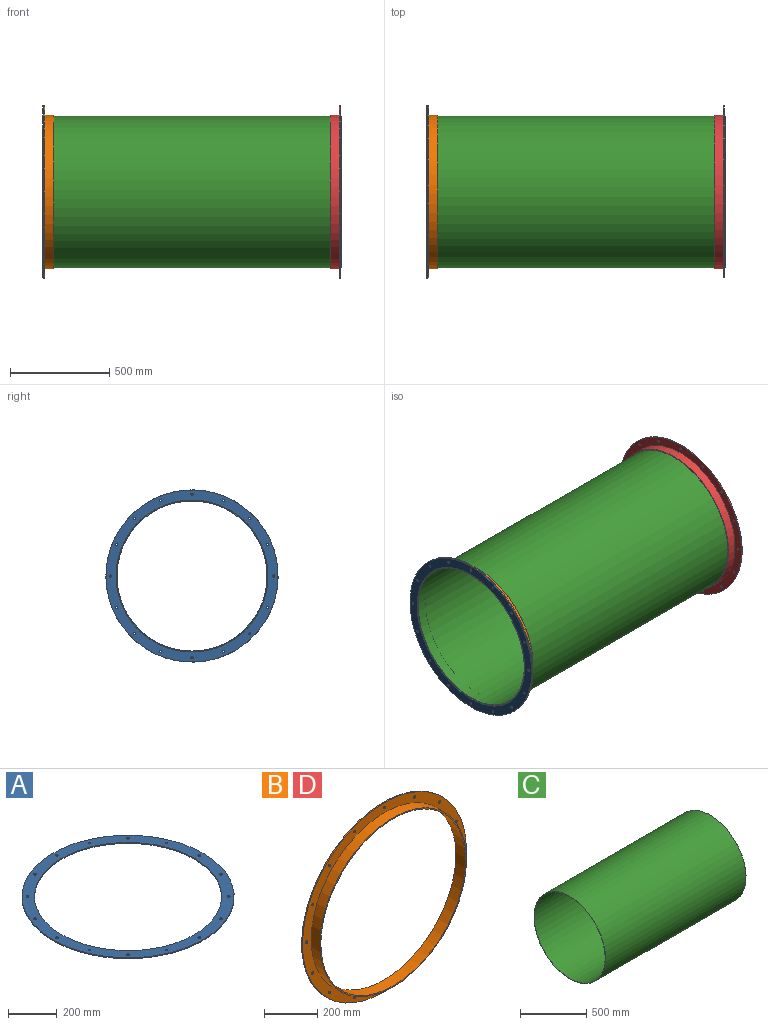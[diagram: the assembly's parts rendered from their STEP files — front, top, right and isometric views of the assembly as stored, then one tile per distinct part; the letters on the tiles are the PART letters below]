
ASSEMBLY  parts=4 mates=3
PART A: 20 faces, bbox 866.9x866.9x4.8 mm
  f0: cylinder r=5.56mm len=11.11mm, axis (0,0,-1), area 166.3mm2, adj f18,f19
  f1: cylinder r=5.56mm len=11.11mm, axis (0,0,-1), area 166.3mm2, adj f18,f19
  f2: cylinder r=5.56mm len=11.11mm, axis (0,0,-1), area 166.3mm2, adj f18,f19
  f3: cylinder r=5.56mm len=11.11mm, axis (0,0,-1), area 166.3mm2, adj f18,f19
  f4: cylinder r=5.56mm len=11.11mm, axis (0,0,-1), area 166.3mm2, adj f18,f19
  f5: cylinder r=5.56mm len=11.11mm, axis (0,0,-1), area 166.3mm2, adj f18,f19
  f6: cylinder r=5.56mm len=11.11mm, axis (0,0,-1), area 166.3mm2, adj f18,f19
  f7: cylinder r=5.56mm len=11.11mm, axis (0,0,-1), area 166.3mm2, adj f18,f19
  f8: cylinder r=5.56mm len=11.11mm, axis (0,0,-1), area 166.3mm2, adj f18,f19
  f9: cylinder r=5.56mm len=11.11mm, axis (0,0,-1), area 166.3mm2, adj f18,f19
  f10: cylinder r=5.56mm len=11.11mm, axis (0,0,-1), area 166.3mm2, adj f18,f19
  f11: cylinder r=5.56mm len=11.11mm, axis (0,0,-1), area 166.3mm2, adj f18,f19
  f12: cylinder r=5.56mm len=11.11mm, axis (0,0,-1), area 166.3mm2, adj f18,f19
  f13: cylinder r=5.56mm len=11.11mm, axis (0,0,-1), area 166.3mm2, adj f18,f19
  f14: cylinder r=5.56mm len=11.11mm, axis (0,0,-1), area 166.3mm2, adj f18,f19
  f15: cylinder r=382.65mm len=765.3mm, axis (0,0,-1), area 11450.3mm2, adj f18,f19
  f16: cylinder r=5.56mm len=11.11mm, axis (0,0,-1), area 166.3mm2, adj f18,f19
  f17: cylinder r=433.45mm len=866.9mm, axis (0,0,-1), area 12970.4mm2, adj f18,f19
  f18: plane 866.9x866.9mm, normal (0,0,1), area 128692.3mm2, adj f0,f1,f2,f3,f4,f5,f6,f7
  f19: plane 866.9x866.9mm, normal (0,0,-1), area 128692.3mm2, adj f0,f1,f2,f3,f4,f5,f6,f7
PART B: 22 faces, bbox 866.9x50.8x866.9 mm
  f0: cylinder r=5.56mm len=11.11mm, axis (0,1,0), area 166.3mm2, adj f17,f18
  f1: cylinder r=5.56mm len=11.11mm, axis (0,1,0), area 166.3mm2, adj f17,f18
  f2: cylinder r=5.56mm len=11.11mm, axis (0,1,0), area 166.3mm2, adj f17,f18
  f3: cylinder r=5.56mm len=11.11mm, axis (0,1,0), area 166.3mm2, adj f17,f18
  f4: cylinder r=5.56mm len=11.11mm, axis (0,1,0), area 166.3mm2, adj f17,f18
  f5: cylinder r=5.56mm len=11.11mm, axis (0,1,0), area 166.3mm2, adj f17,f18
  f6: cylinder r=5.56mm len=11.11mm, axis (0,1,0), area 166.3mm2, adj f17,f18
  f7: cylinder r=5.56mm len=11.11mm, axis (0,1,0), area 166.3mm2, adj f17,f18
  f8: cylinder r=5.56mm len=11.11mm, axis (0,1,0), area 166.3mm2, adj f17,f18
  f9: cylinder r=5.56mm len=11.11mm, axis (0,1,0), area 166.3mm2, adj f17,f18
  f10: cylinder r=5.56mm len=11.11mm, axis (0,1,0), area 166.3mm2, adj f17,f18
  f11: cylinder r=5.56mm len=11.11mm, axis (0,1,0), area 166.3mm2, adj f17,f18
  f12: cylinder r=5.56mm len=11.11mm, axis (0,1,0), area 166.3mm2, adj f17,f18
  f13: cylinder r=5.56mm len=11.11mm, axis (0,1,0), area 166.3mm2, adj f17,f18
  f14: cylinder r=5.56mm len=11.11mm, axis (0,1,0), area 166.3mm2, adj f17,f18
  f15: cylinder r=5.56mm len=11.11mm, axis (0,1,0), area 166.3mm2, adj f17,f18
  f16: cylinder r=433.45mm len=866.9mm, axis (0,1,0), area 12970.4mm2, adj f17,f18
  f17: plane 866.9x866.9mm, normal (0,-1,0), area 117170.7mm2, adj f0,f1,f2,f3,f4,f5,f6,f7
  f18: plane 866.9x866.9mm, normal (0,1,0), area 128692.3mm2, adj f0,f1,f2,f3,f4,f5,f6,f7
  f19: cylinder r=382.65mm len=765.3mm, axis (0,1,0), area 122136.8mm2, adj f18,f21
  f20: cylinder r=387.41mm len=774.83mm, axis (0,1,0), area 112064.1mm2, adj f17,f21
  f21: plane 774.83x774.83mm, normal (0,-1,0), area 11521.6mm2, adj f19,f20
PART C: 4 faces, bbox 1498.6x762x762 mm
  f0: plane 762x762mm, normal (1,0,0), area 8141.6mm2, adj f1,f2
  f1: cylinder r=377.58mm len=1498.6mm, axis (-1,0,0), area 3555321.1mm2, adj f0,f3
  f2: cylinder r=381mm len=1498.6mm, axis (-1,0,0), area 3587489mm2, adj f0,f3
  f3: plane 762x762mm, normal (-1,0,0), area 8141.6mm2, adj f1,f2
PART D: same geometry as B
PLACE A rot(axis=(0.71,0,0.71),180deg) t=(-383.98,196.63,-23.49)mm
PLACE B rot(axis=(0.58,-0.58,0.58),120deg) t=(-379.22,196.63,-23.49)mm
PLACE C t=(-381.6,196.63,-23.49)mm
PLACE D rot(axis=(0.58,0.58,-0.58),120deg) t=(1113.83,196.63,-23.49)mm
MATE fastened D.f19 <-> C.f2  axis (1,0,0) through (1113.83,196.63,-23.49)mm
MATE fastened A.f15 <-> B.f19  axis (1,0,0) through (-379.22,196.63,-23.49)mm
MATE fastened A.f15 <-> C.f2  axis (-1,0,0) through (-381.6,196.63,-23.49)mm
